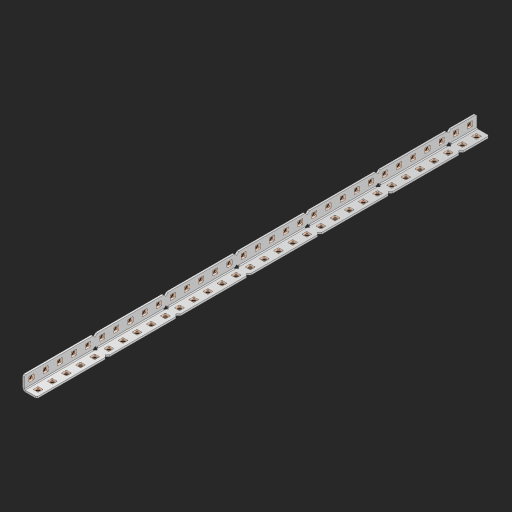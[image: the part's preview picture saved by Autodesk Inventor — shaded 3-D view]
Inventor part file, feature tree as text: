
AUTODESK INVENTOR PART (.ipt)
format: ipt  version: 2023 (Build 270158000, 158)  size: 1,075,200 bytes
history: native  units: in
note: dims shown in document units (in); Inventor stores cm internally (conversion verified against a paired STEP export)
features: other x70, extrude x65, sheet_metal_op x8, sketch x5, pattern_linear x1, mirror x1, chamfer x1
ambient origin geometry x8: Origin, YZ Plane, XZ Plane, XY Plane, X Axis, Y Axis, Z Axis, Center Point
bodies: Solid1 (feature_tree), Body (feature_tree)
feature tree (151):
  sheet_metal_op  "Flanges"
  sheet_metal_op  "Body Pattern"
  other  "Arc Length"
  pattern_linear  "Notch Pattern"  Spacing1=0.125in  [1 undecoded]
  other  "Diagonal Plane"
  mirror  "Everything Mirrored"
  chamfer  "End Chamfer"
  sketch  "Sketch1"  dims[d0=0.5in]
  other  "Plate1"
  sketch  "Sketch2"  dims[d1=16.0in]
  other  "Plate2"
  sheet_metal_op  "Bend1"
  sheet_metal_op  "Corner1"
  sketch  "Sketch8"  dims[d2=0.0625in]
  sketch  "Sketch9"  dims[d3=0.0625in]
  other  "Srf91"
  sheet_metal_op  "Body Pattern Sketch"
  other  "Srf92"
  sketch  "Sketch13"  dims[d4=0.0312in d5=0.125in d6=0.0625in d7=0.5in d8=90.0deg d9=0.0312in d10=0.25in d11=0.0625in d12=0.0625in d49=0.182in d50=0.02in d52=0.25in d53=0.0625in d54=0.0in d55=0.172in d56=1.0in d57=0.0in d85=0.1473in d86=0.1782in d89=0.0625in d90=0.0in d91=0.04in d92=0.0491in d95=2.5in d96=0.04in d97=0.25in d98=45.0deg d123=0.204in d126=0.0491in d127=0.1473in d128=0.08in d129=0.04in d130=2.5in d131=12.5984in d133=0.5in d134=0.3937in d136=1.0in]
  other  "Srf856"
  other  "Srf857"
  other  "Srf858"
  other  "Srf859"
  other  "Srf860"
  other  "Srf861"
  other  "Srf1275"
  other  "Srf1276"
  other  "Srf1278"
  other  "Srf1279"
  other  "Srf1280"
  other  "Srf1281"
  other  "Srf1282"
  other  "Srf1283"
  other  "Srf1383"
  other  "Srf1384"
  other  "Srf1385"
  other  "Srf1386"
  other  "Srf1387"
  other  "Srf1388"
  other  "Srf1389"
  other  "Srf1390"
  other  "Srf1391"
  other  "Srf1392"
  other  "Srf1393"
  other  "Srf1394"
  other  "Srf1395"
  other  "Srf1396"
  other  "Srf1397"
  other  "Srf1398"
  other  "Srf1399"
  other  "Srf1400"
  other  "Srf1401"
  other  "Srf1402"
  other  "Srf1403"
  other  "Srf1404"
  other  "Srf1405"
  other  "Srf1406"
  other  "Srf1407"
  other  "Srf1475"
  other  "Srf1476"
  other  "Srf1477"
  other  "Srf1478"
  other  "Srf1479"
  other  "Srf1480"
  other  "Srf1481"
  other  "Srf1482"
  other  "Srf1483"
  other  "Srf1484"
  other  "Srf1485"
  other  "Srf1486"
  other  "Srf1487"
  other  "Srf1488"
  other  "Srf1489"
  other  "Srf1490"
  other  "Srf1491"
  other  "Srf1492"
  other  "Srf1493"
  other  "Srf1494"
  other  "Srf1495"
  other  "Srf1496"
  other  "Srf1497"
  other  "Srf1498"
  other  "Srf1499"
  sheet_metal_op  "Body Stamp"
  sheet_metal_op  "Body Circle"
  sheet_metal_op  "Notch"
  extrude  "ExtrusionSrf92"  Depth=0.0625in
  extrude  "ExtrusionSrf856"  Depth=0.5in TaperAngle=90.0deg
  extrude  "ExtrusionSrf857"  Depth=0.25in
  extrude  "ExtrusionSrf858"  Depth=0.0625in
  extrude  "ExtrusionSrf859"  Depth=0.0625in
  extrude  "ExtrusionSrf860"  Depth=0.3937in
  extrude  "ExtrusionSrf861"  Depth=0.02in
  extrude  "ExtrusionSrf1275"  Depth=0.25in
  extrude  "ExtrusionSrf1276"  Depth=0.0625in
  extrude  "ExtrusionSrf1277"  TaperAngle=0.0deg  [1 undecoded]
  extrude  "ExtrusionSrf1278"  Depth=0.3937in
  extrude  "ExtrusionSrf1279"  Depth=0.3937in TaperAngle=0.0deg
  extrude  "ExtrusionSrf1280"  Depth=0.3937in
  extrude  "ExtrusionSrf1281"  Depth=0.3937in
  extrude  "ExtrusionSrf1282"  Depth=0.0625in
  extrude  "ExtrusionSrf1383"  Depth=0.3937in TaperAngle=0.0deg
  extrude  "ExtrusionSrf1384"  Depth=0.3937in
  extrude  "ExtrusionSrf1385"  Depth=0.25in TaperAngle=45.0deg
  extrude  "ExtrusionSrf1386"  Depth=0.3937in
  extrude  "ExtrusionSrf1387"  Depth=0.3937in
  extrude  "ExtrusionSrf1388"  Depth=0.3937in
  extrude  "ExtrusionSrf1389"  Depth=0.3937in
  extrude  "ExtrusionSrf1390"  Depth=0.3937in
  extrude  "ExtrusionSrf1391"  Depth=0.3937in
  extrude  "ExtrusionSrf1392"  Depth=0.3937in
  extrude  "ExtrusionSrf1393"  Depth=0.5in
  extrude  "ExtrusionSrf1394"  [1 undecoded]
  extrude  "ExtrusionSrf1395"  [1 undecoded]
  extrude  "ExtrusionSrf1396"  [1 undecoded]
  extrude  "ExtrusionSrf1397"  [1 undecoded]
  extrude  "ExtrusionSrf1398"  [1 undecoded]
  extrude  "ExtrusionSrf1399"  [1 undecoded]
  extrude  "ExtrusionSrf1400"  [1 undecoded]
  extrude  "ExtrusionSrf1401"  [1 undecoded]
  extrude  "ExtrusionSrf1402"  [1 undecoded]
  extrude  "ExtrusionSrf1403"  [1 undecoded]
  extrude  "ExtrusionSrf1404"  [1 undecoded]
  extrude  "ExtrusionSrf1405"  [1 undecoded]
  extrude  "ExtrusionSrf1406"  [1 undecoded]
  extrude  "ExtrusionSrf1407"  [1 undecoded]
  extrude  "ExtrusionSrf1475"  [1 undecoded]
  extrude  "ExtrusionSrf1476"  [1 undecoded]
  extrude  "ExtrusionSrf1477"  [1 undecoded]
  extrude  "ExtrusionSrf1478"  [1 undecoded]
  extrude  "ExtrusionSrf1479"  [1 undecoded]
  extrude  "ExtrusionSrf1480"  [1 undecoded]
  extrude  "ExtrusionSrf1481"  [1 undecoded]
  extrude  "ExtrusionSrf1482"  [1 undecoded]
  extrude  "ExtrusionSrf1483"  [1 undecoded]
  extrude  "ExtrusionSrf1484"  [1 undecoded]
  extrude  "ExtrusionSrf1485"  [1 undecoded]
  extrude  "ExtrusionSrf1486"  [1 undecoded]
  extrude  "ExtrusionSrf1487"  [1 undecoded]
  extrude  "ExtrusionSrf1488"  [1 undecoded]
  extrude  "ExtrusionSrf1489"  [1 undecoded]
  extrude  "ExtrusionSrf1490"  [1 undecoded]
  extrude  "ExtrusionSrf1491"  [1 undecoded]
  extrude  "ExtrusionSrf1492"  [1 undecoded]
  extrude  "ExtrusionSrf1493"  [1 undecoded]
  extrude  "ExtrusionSrf1494"  [1 undecoded]
  extrude  "ExtrusionSrf1495"  [1 undecoded]
  extrude  "ExtrusionSrf1496"  [1 undecoded]
  extrude  "ExtrusionSrf1497"  [1 undecoded]
  extrude  "ExtrusionSrf1498"  [1 undecoded]
  extrude  "ExtrusionSrf1499"  [1 undecoded]
note: 41 required parameter values undecoded (feature->parameter linkage not recoverable at this tier; creation-order binding heuristic only, values carry confidence <= 0.55)
